# Revit family: Thorium-Noytron
name_source: partatom
category: Furniture
units: mm (PartAtom-declared; Revit-internal decimal feet)

## family parameters
Always vertical = Yes
Cut with Voids When Loaded = No
OmniClass Number = 23.40.10.21.27
OmniClass Title = Exterior Athletic Equipment
Room Calculation Point = No
Shared = No
Work Plane-Based = Yes

## types (2) — shared parameters
Concrete foundation / Surface mounting = Yes
Critical falling height (mm) = 2750 mm  [stored 9.02231 ft]
Manufacturer = Sove As
Minimum required safety area (m2) = 43,8
Model name = Thorium Noytron
Safety area visibility = Yes
Stolpe 110 / 1 = Aluminum RAL9022
Svanemerke / Nordic EcoLabel = Yes
Type Comments = L=6500, W=7500, H=4400
URL = https://sove.no
zero-valued in all types: Default Elevation

## per-type parameters (varying)
| type | Crossbar 1 | Model |
| Thorium Noytron | Aluminum RAL6018 | 14-200-020 |
| ChooseYourColor | Aluminum RAL-ChooseYourColor | S14-200-020 |

note: [stored X ft] marks values corroborated as IEEE doubles in the binary element streams (Revit-internal decimal feet)

## geometry (parser evidence)
native form markers: Sweep x28
no freeform markers — native parametric forms only
